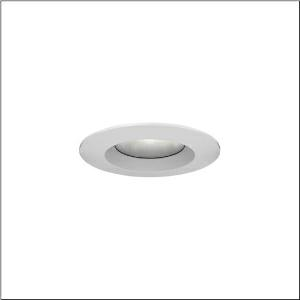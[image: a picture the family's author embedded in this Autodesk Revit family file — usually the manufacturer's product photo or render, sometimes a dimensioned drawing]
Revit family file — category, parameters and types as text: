
# Revit family: lunis_40_ip65_5dp10c72v365
name_source: partatom
category: Lighting Fixtures
units: mm (PartAtom-declared; Revit-internal decimal feet)

## family parameters
Cut with Voids When Loaded = No
Host = Face
Light Source = No
Part Type = Normal
Room Calculation Point = No
Round Connector Dimension = Use Diameter
Shared = No

## types (1)
- Lunis 40 IP65 (1 x LED, 350 lm, 3.5 W, 3000K)
    Apparent Load = 4 VA
    CIE Flux Codes = 57 88 99 100 100
    Color Rendering = 80
    Color Temperature = 3000K
    Default Elevation = 1800 mm
    Description = Lunis 40 IP65, downlight, of PMMA, light emission: direct distribution, LED rated luminous flux: 350lm, light colour: 830, control gear: ECG, mains connection: 220..240V, AC, 50/60Hz, housing, round, of aluminium, coated, traffic white (RAL 9016), diameter: 83mm, recess depth: 43mm, protection rating (complete): IP20, protection rating (on room side): IP65, insulation class (complete): insulation class II (safety insulation), certification: CE, permissible ambient temperature for indoor applications: -20..+40°C, packaging unit: 1 piece
    Height = 0 mm  [stored 0 ft]
    Lamp = 1 x LED
    Lamp Light Flux = 350 lm
    Lamp Power = 3.5 W
    Lamp count = 1
    Length = 83 mm
    Luminous efficacy = 100 lm/W
    Manufacturer = Siteco
    ModVariant = No
    Model = 5DP10C72V365
    Mounting Place = Ceiling
    Mounting Type = Recessed
    Number of Poles = 1
    OnlyDefault = Yes
    Power Factor = 1
    Product Name = Lunis 40 IP65
    Product group = downlight
    ProductGroupID = 400
    Protection Class = Protection class II
    Protection Degree = IP 20
    RLX_Detail_Level = 1
    RLX_Emergency_Light_Flux = 0 lm
    RLX_Emergency_Type = 0
    RLX_Emergency_Type_DB = No
    RlxData = <blob elided: 24021 chars, md5=e6f5eafd>
    Socket = socket
    Standby Power = 0 W
    System Light Flux = 350 lm
    System Power = 4 W
    Type Comments = Product without accessories
    Type Image = l_1006628.jpg
    URL = http://relux.com
    VarID = ---
    Voltage = 0 V
    Weight = 0.00 kg
    Width = 0 mm  [stored 0 ft]

note: [stored X ft] marks values corroborated as IEEE doubles in the binary element streams (Revit-internal decimal feet)

## geometry (parser evidence)
native form markers: Blend x4, Sweep x9
no freeform markers — native parametric forms only
